# Revit family: 873-00-001-DN80-200
name_source: partatom
category: Pipe Accessories
units: mm (PartAtom-declared; Revit-internal decimal feet)

## family parameters
Always vertical = Yes
Cut with Voids When Loaded = No
Part Type = Valve - Breaks Into
Round Connector Dimension = Use Diameter
Shared = No
Work Plane-Based = No

## types (5) — shared parameters
873-0080-00-141000 = DN80_PN16
873-0100-00-141000 = DN100_PN16
873-0125-00-141000 = DN125_PN16
873-0150-00-141000 = DN150_PN16
873-0200-00-041000 = DN200_PN10
Body_Wallthicknss = 10 mm  [stored 0.0328084 ft]
Description_ = AVK DISMANTLING JOINT
Flange_thickness = 20 mm  [stored 0.0656168 ft]
Search_table = 873-00-001-DN80-200
URL product pages = https://www.avkvalves.com

## per-type parameters (varying)
| type | A | DN | Id(Radius) | L | T | d1 | d2 |
| DN080 | 200 mm  [stored 0.656168 ft] | 80 mm  [stored 0.262467 ft] | 40 mm  [stored 0.131234 ft] | 340 mm  [stored 1.11549 ft] | 16 mm  [stored 0.0524934 ft] | 160 mm  [stored 0.524934 ft] | 100 mm  [stored 0.328084 ft] |
| DN100 | 200 mm  [stored 0.656168 ft] | 100 mm  [stored 0.328084 ft] | 50 mm  [stored 0.164042 ft] | 340 mm  [stored 1.11549 ft] | 16 mm  [stored 0.0524934 ft] | 180 mm  [stored 0.590551 ft] | 110 mm  [stored 0.360892 ft] |
| DN125 | 200 mm  [stored 0.656168 ft] | 125 mm  [stored 0.410105 ft] | 63 mm | 340 mm  [stored 1.11549 ft] | 16 mm  [stored 0.0524934 ft] | 210 mm  [stored 0.688976 ft] | 125 mm  [stored 0.410105 ft] |
| DN150 | 200 mm  [stored 0.656168 ft] | 150 mm  [stored 0.492126 ft] | 75 mm | 350 mm  [stored 1.14829 ft] | 20 mm  [stored 0.0656168 ft] | 240 mm  [stored 0.787402 ft] | 143 mm |
| DN200 | 210 mm  [stored 0.688976 ft] | 200 mm  [stored 0.656168 ft] | 100 mm  [stored 0.328084 ft] | 350 mm  [stored 1.14829 ft] | 20 mm  [stored 0.0656168 ft] | 295 mm  [stored 0.967848 ft] | 170 mm  [stored 0.557743 ft] |

note: [stored X ft] marks values corroborated as IEEE doubles in the binary element streams (Revit-internal decimal feet)

## geometry (parser evidence)
native form markers: Sweep x3
no freeform markers — native parametric forms only
